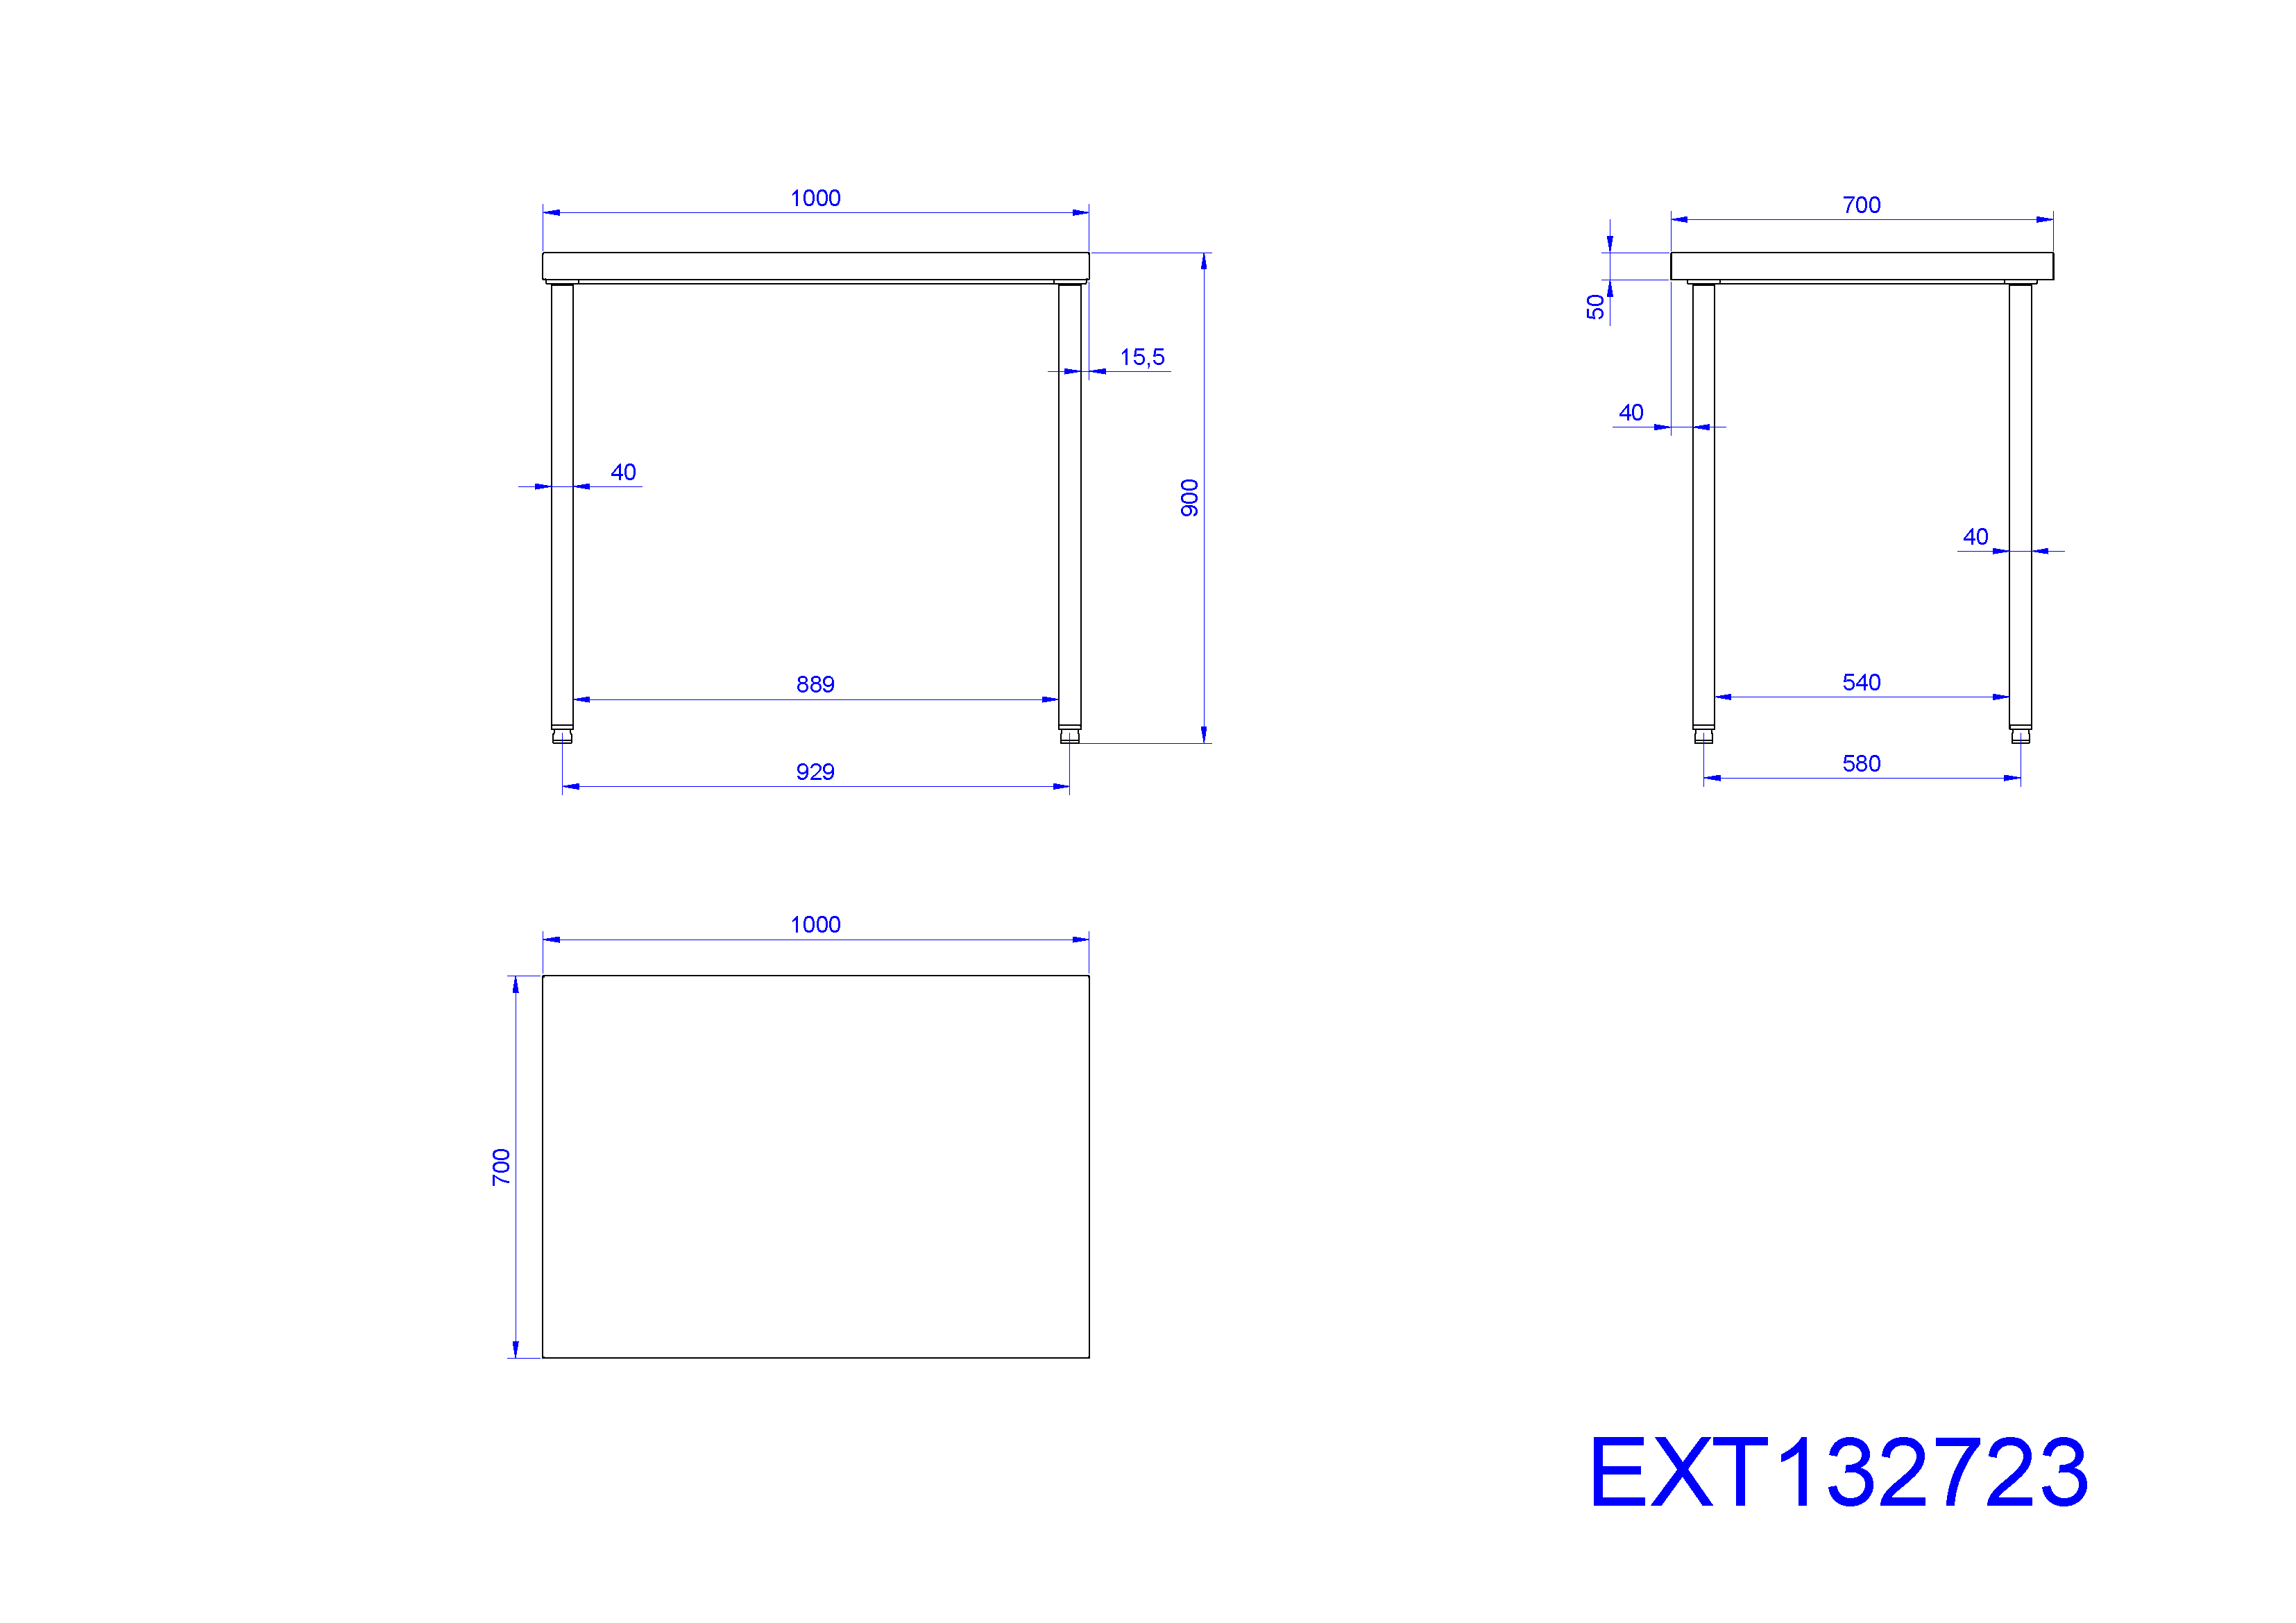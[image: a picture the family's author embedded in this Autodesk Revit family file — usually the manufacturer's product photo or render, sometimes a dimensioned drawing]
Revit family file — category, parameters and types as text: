
# Revit family: QF_ELECTROLUXPROFESSIONAL_132817_MLA716PN
name_source: partatom
category: Attrezzature speciali
units: mm (PartAtom-declared; Revit-internal decimal feet)

## family parameters
Basato su piano di lavoro = No
Condiviso = No
Punto di calcolo locali = No
Quota connettore circolare = Usa diametro
Sempre verticale = Sì
Taglio con vuoti quando caricato = No
Tipo di parte = Normale

## types (1)
- Standard
    Accessory = Sì
    Cold Water Size = 0 mm
    Compressed Air Pressure = 0.0 Pa
    Compressed Air Size = 0 mm
    Compressed Air Volume = 0.0 L/s
    Condensate Return Size = 0 mm
    Cycle = 0 Hz
    Depth Actual = 700 mm  [stored 2.29659 ft]
    Descrizione = CUPBOARD SINK 1 BOWL(500X500) 2 DOOR 700MM
    Direct Waste Size = 51 mm
    Gas Input Pressure = 0
    Gas KW = 0
    Gas Size = 0 mm
    HP = 0 HP
    Height Actual = 1000 mm  [stored 3.28084 ft]
    Hot Water Size = 0 mm
    Item Number = 132817
    Length Actual = 700 mm  [stored 2.29659 ft]
    Modello = MLA716PN
    Phase = 0
    Produttore = Electrolux Professional
    Prospetto di default = 0 mm  [stored 0 ft]
    Refrigerant Compressor Remote = Sì
    Refrigeration Liquid Line Size = 0 mm  [stored 0 ft]
    Refrigeration Suction Line Size = 0 mm  [stored 0 ft]
    Steam Consumption per Hour = 0
    Steam Supply Maximum Pressure = 0.0 Pa
    Steam Supply Minimum Pressure = 0.0 Pa
    Steam Supply Size = 0 mm
    URL = https://www.electroluxprofessional.com
    URL Manufacturer = https://www.electroluxprofessional.com
    Volts = 0 V
    Watts = 0 W
    Weight = 40.00 kg

note: source unit labels omitted for Gas Input Pressure — the stored unit's dimension contradicts the parameter name (converter mislabeling)

note: [stored X ft] marks values corroborated as IEEE doubles in the binary element streams (Revit-internal decimal feet)

## geometry (parser evidence)
native form markers: Sweep x2
no freeform markers — native parametric forms only
